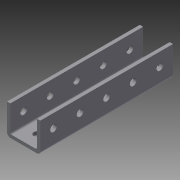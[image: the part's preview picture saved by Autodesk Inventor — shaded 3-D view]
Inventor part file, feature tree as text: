
AUTODESK INVENTOR PART (.ipt)
format: ipt  version: 2014 (Build 180170000, 170)  size: 120,832 bytes
history: native  units: in
note: dims shown in document units (in); Inventor stores cm internally (conversion verified against a paired STEP export)
features: sketch x3, hole x2, extrude x1, pattern_linear x1
ambient origin geometry x8: Origin, YZ Plane, XZ Plane, XY Plane, X Axis, Y Axis, Z Axis, Center Point
bodies: Solid1 (feature_tree)
feature tree (7):
  extrude  "Extrusion1"  Depth=5.0in TaperAngle=0.0deg
  sketch  "Sketch2"  dims[d6=0.5in d7=0.5in]
  sketch  "Sketch3"  dims[d8=0.25in d9=0.75in d10=0.375in d11=0.25in d12=0.5635in d13=1.0in d14=0.8108in d15=0.25in d16=0.75in d17=0.375in d18=0.25in d19=0.5635in d20=1.0in d21=0.8108in d22=1.9685in d24=1.0in]
  hole  "Hole1"  [1 undecoded]
  hole  "Hole2"  [1 undecoded]
  pattern_linear  "Rectangular Pattern1"  [2 undecoded]
  sketch  "Sketch1"  dims[d0=1.25in d1=1.125in d2=0.0625in d3=0.125in d4=5.0in d5=0.0in]
note: 4 required parameter values undecoded (feature->parameter linkage not recoverable at this tier; creation-order binding heuristic only, values carry confidence <= 0.55)
